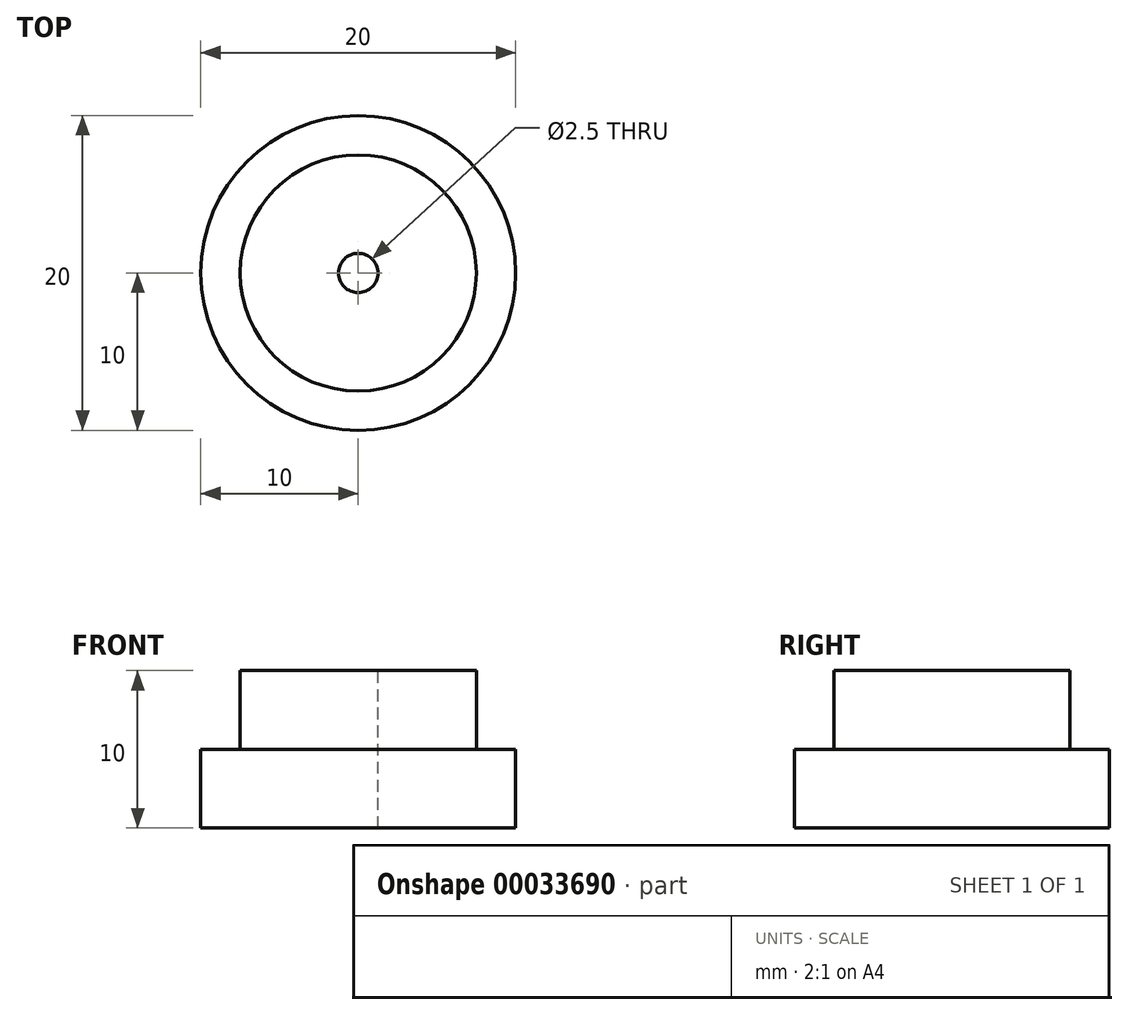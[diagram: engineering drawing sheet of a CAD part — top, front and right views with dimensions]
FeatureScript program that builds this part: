
annotation { "Feature Type Name" : "Feature", "Feature Type Description" : "" }
export const myFeature = defineFeature(function(context is Context, id is Id, definition is map)
    precondition{}
    {
        {
            var Q0;
            Q0=qCreatedBy(makeId("Top.planeOp"),FACE);
            var sketch = newSketch(context, id + "F0", { "sketchPlane" : qUnion([Q0])});
            skCircle(sketch, "E0", {"center": v(0, 0) * mm, "radius": 7.5 * mm});
            skCircle(sketch, "E1", {"center": v(0, 0) * mm, "radius": 10 * mm});
            skSolve(sketch);
        }
        {
            var Q0;
            Q0=qSketchRegion(id+"F0",true);
            var Q1;
            Q1=makeQuery(id+"F0.imprint","IMPRINT",FACE,{"disambiguationData":[TD([[makeQuery(id+"F0.imprint","IMPRINT",EDGE,{"derivedFrom":sQuery(id+"F0.wireOp",EDGE,"E0")}),1.0]])]});
            extrude(context, id + "F1", {"entities" : qUnion([Q0, Q1]), "depth" : 5 * mm});
        }
        {
            var Q0;
            Q0=makeQuery(id+"F1.opExtrude","CAP_FACE",FACE,{"disambiguationData":[OSD([sQuery(id+"F0.wireOp",EDGE,"E1")])],"isStart":false});
            var sketch = newSketch(context, id + "F2", { "sketchPlane" : qUnion([Q0])});
            skCircle(sketch, "E2", {"center": v(0, 0) * mm, "radius": 7.5 * mm});
            skSolve(sketch);
        }
        {
            var Q0;
            Q0=qSketchRegion(id+"F2",true);
            extrude(context, id + "F3", {"entities" : qUnion([Q0]), "operationType" : NewBodyOperationType.ADD, "depth" : 5 * mm});
        }
        {
            var Q0;
            Q0=makeQuery(id+"F3.opExtrude","CAP_FACE",FACE,{"disambiguationData":[OSD([sQuery(id+"F2.wireOp",EDGE,"E2")])],"isStart":false});
            var sketch = newSketch(context, id + "F4", { "sketchPlane" : qUnion([Q0])});
            skCircle(sketch, "E3", {"center": v(0, 0) * mm, "radius": 1.25 * mm});
            skSolve(sketch);
        }
        {
            var Q0;
            Q0=makeQuery(id+"F4.imprint","IMPRINT",FACE,{"disambiguationData":[TD([[makeQuery(id+"F4.imprint","IMPRINT",EDGE,{"derivedFrom":sQuery(id+"F4.wireOp",EDGE,"E3")}),1.0]])]});
            var Q1;
            Q1=sQuery(id+"F4.wireOp",EDGE,"E3");
            extrude(context, id + "F5", {"entities" : qUnion([Q0]), "operationType" : NewBodyOperationType.REMOVE, "surfaceEntities" : qUnion([Q1]), "oppositeDirection" : true, "depth" : 25.4 * mm});
        }
    });
